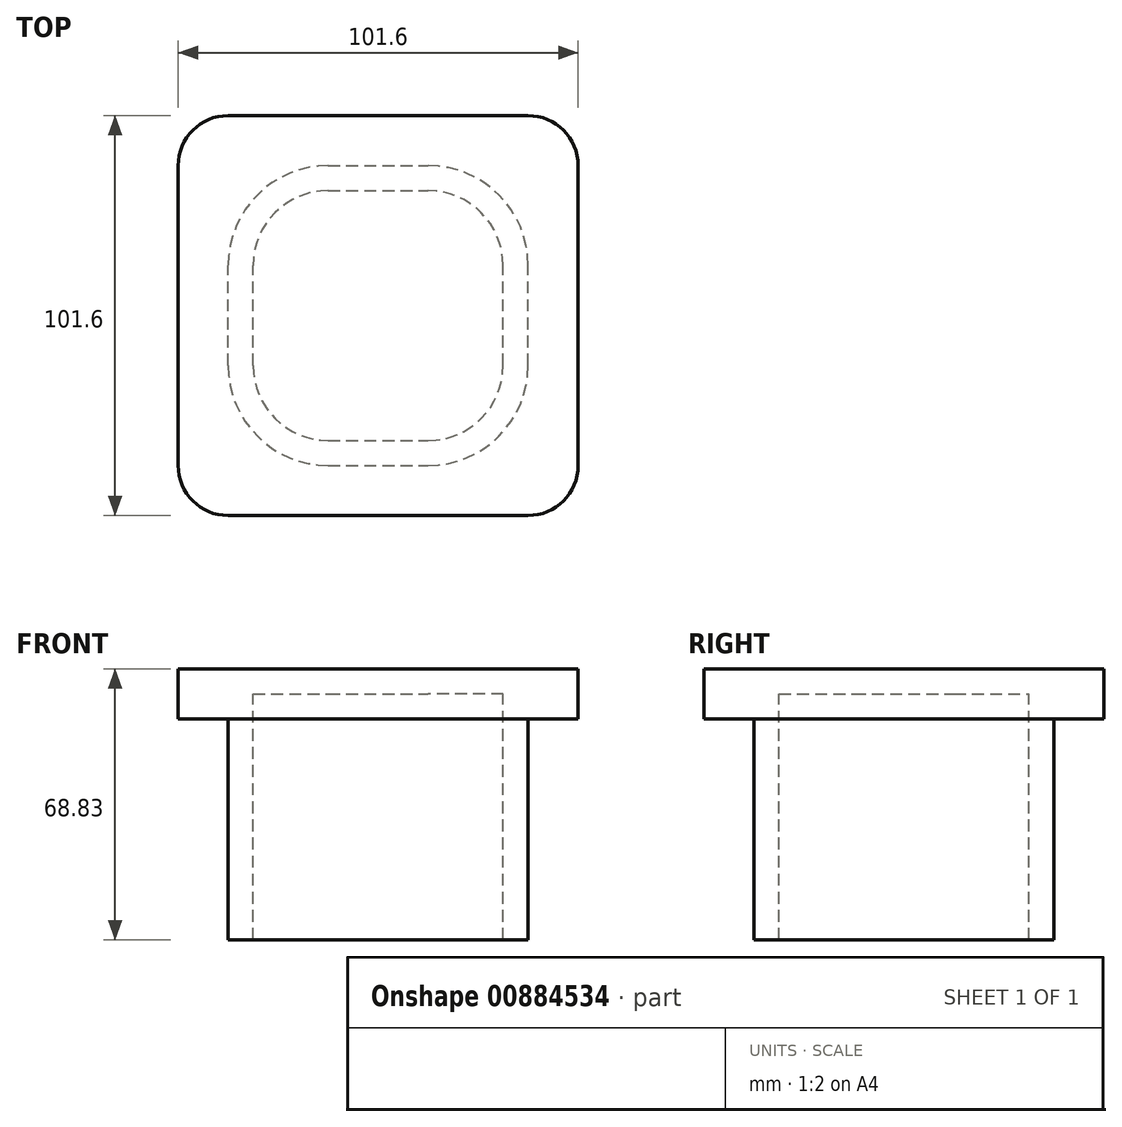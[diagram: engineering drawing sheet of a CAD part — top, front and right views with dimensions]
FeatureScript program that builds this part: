
annotation { "Feature Type Name" : "Feature", "Feature Type Description" : "" }
export const myFeature = defineFeature(function(context is Context, id is Id, definition is map)
    precondition{}
    {
        {
            var Q0;
            Q0=qCreatedBy(makeId("Top.planeOp"),FACE);
            var sketch = newSketch(context, id + "F0", { "sketchPlane" : qUnion([Q0])});
            skLineSegment(sketch, "E0.bottom", {"start": v(-12.7, -38.1) * mm, "end": v(12.7, -38.1) * mm});
            skLineSegment(sketch, "E0.top", {"start": v(-12.7, 38.1) * mm, "end": v(12.7, 38.1) * mm});
            skLineSegment(sketch, "E0.left", {"start": v(-38.1, -12.7) * mm, "end": v(-38.1, 12.7) * mm});
            skLineSegment(sketch, "E0.right", {"start": v(38.1, -12.7) * mm, "end": v(38.1, 12.7) * mm});
            skPoint(sketch, "E0.middle", {"position": v(0, 0) * mm});
            skPoint(sketch, "E1.visualSharp", {"position": v(-38.1, 38.1) * mm});
            skArc(sketch, "E1.filletArc", {"start": v(-12.7, 38.1) * mm, "mid": v(-30.66, 30.66) * mm, "end": v(-38.1, 12.7) * mm});
            skPoint(sketch, "E2.visualSharp", {"position": v(-38.1, -38.1) * mm});
            skArc(sketch, "E2.filletArc", {"start": v(-38.1, -12.7) * mm, "mid": v(-30.66, -30.66) * mm, "end": v(-12.7, -38.1) * mm});
            skPoint(sketch, "E3.visualSharp", {"position": v(38.1, -38.1) * mm});
            skArc(sketch, "E3.filletArc", {"start": v(12.7, -38.1) * mm, "mid": v(30.66, -30.66) * mm, "end": v(38.1, -12.7) * mm});
            skPoint(sketch, "E4.visualSharp", {"position": v(38.1, 38.1) * mm});
            skArc(sketch, "E4.filletArc", {"start": v(38.1, 12.7) * mm, "mid": v(30.66, 30.66) * mm, "end": v(12.7, 38.1) * mm});
            skSolve(sketch);
        }
        {
            var Q0;
            Q0=makeQuery(id+"F0.imprint","IMPRINT",FACE,{"disambiguationData":[TD([[makeQuery(id+"F0.imprint","IMPRINT",EDGE,{"derivedFrom":sQuery(id+"F0.wireOp",EDGE,"E0.bottom")}),1.0]])]});
            extrude(context, id + "F1", {"entities" : qUnion([Q0]), "depth" : 56.13 * mm, "offsetDistance" : 25.4 * mm});
        }
        {
            var Q0;
            Q0=makeQuery(id+"F1.opExtrude","CAP_FACE",FACE,{"disambiguationData":[OSD([sQuery(id+"F0.wireOp",EDGE,"E0.bottom"),sQuery(id+"F0.wireOp",EDGE,"E0.top"),sQuery(id+"F0.wireOp",EDGE,"E0.left"),sQuery(id+"F0.wireOp",EDGE,"E0.right"),sQuery(id+"F0.wireOp",EDGE,"E1.filletArc"),sQuery(id+"F0.wireOp",EDGE,"E2.filletArc"),sQuery(id+"F0.wireOp",EDGE,"E3.filletArc"),sQuery(id+"F0.wireOp",EDGE,"E4.filletArc"),sQuery(id+"F0.wireOp",EDGE,"D1Bg6Gvg-mNT8-uoGM-i0QS-vutlQdIsJS7o")])],"isStart":false});
            var sketch = newSketch(context, id + "F2", { "sketchPlane" : qUnion([Q0])});
            skLineSegment(sketch, "E5.bottom", {"start": v(-38.1, -50.8) * mm, "end": v(38.1, -50.8) * mm});
            skLineSegment(sketch, "E5.top", {"start": v(-38.1, 50.8) * mm, "end": v(38.1, 50.8) * mm});
            skLineSegment(sketch, "E5.left", {"start": v(-50.8, -38.1) * mm, "end": v(-50.8, 38.1) * mm});
            skLineSegment(sketch, "E5.right", {"start": v(50.8, -38.1) * mm, "end": v(50.8, 38.1) * mm});
            skPoint(sketch, "E5.middle", {"position": v(0, 0) * mm});
            skPoint(sketch, "E6.visualSharp", {"position": v(-50.8, 50.8) * mm});
            skArc(sketch, "E6.filletArc", {"start": v(-38.1, 50.8) * mm, "mid": v(-47.08, 47.08) * mm, "end": v(-50.8, 38.1) * mm});
            skPoint(sketch, "E7.visualSharp", {"position": v(-50.8, -50.8) * mm});
            skArc(sketch, "E7.filletArc", {"start": v(-50.8, -38.1) * mm, "mid": v(-47.08, -47.08) * mm, "end": v(-38.1, -50.8) * mm});
            skPoint(sketch, "E8.visualSharp", {"position": v(50.8, -50.8) * mm});
            skArc(sketch, "E8.filletArc", {"start": v(38.1, -50.8) * mm, "mid": v(47.08, -47.08) * mm, "end": v(50.8, -38.1) * mm});
            skPoint(sketch, "E9.visualSharp", {"position": v(50.8, 50.8) * mm});
            skArc(sketch, "E9.filletArc", {"start": v(50.8, 38.1) * mm, "mid": v(47.08, 47.08) * mm, "end": v(38.1, 50.8) * mm});
            skSolve(sketch);
        }
        {
            var Q0;
            Q0 = qSketchRegion(id + "F2", true);
            extrude(context, id + "F3", {"entities" : qUnion([Q0]), "operationType" : NewBodyOperationType.ADD, "depth" : 12.7 * mm, "offsetDistance" : 25.4 * mm});
        }
        {
            var Q0;
            Q0=makeQuery(id+"F1.opExtrude","CAP_FACE",FACE,{"disambiguationData":[OSD([sQuery(id+"F0.wireOp",EDGE,"E0.bottom"),sQuery(id+"F0.wireOp",EDGE,"E0.top"),sQuery(id+"F0.wireOp",EDGE,"E0.left"),sQuery(id+"F0.wireOp",EDGE,"E0.right"),sQuery(id+"F0.wireOp",EDGE,"E1.filletArc"),sQuery(id+"F0.wireOp",EDGE,"E2.filletArc"),sQuery(id+"F0.wireOp",EDGE,"E3.filletArc"),sQuery(id+"F0.wireOp",EDGE,"E4.filletArc")])],"isStart":true});
            shell(context, id + "F4", {"entities" : qUnion([Q0]), "thickness" : 6.35 * mm});
        }
    });
